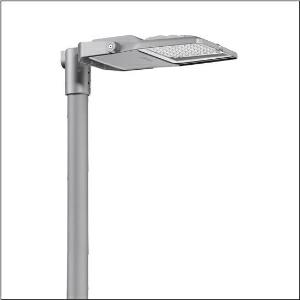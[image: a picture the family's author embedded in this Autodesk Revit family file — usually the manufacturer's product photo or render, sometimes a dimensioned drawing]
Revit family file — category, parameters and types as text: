
# Revit family: floodlight_fl_21_iq_mini___pl64_5xa7771d2e3a_d262
name_source: partatom
category: Lighting Fixtures
units: mm (PartAtom-declared; Revit-internal decimal feet)

## family parameters
Cut with Voids When Loaded = No
Host = Face
Light Source = No
Part Type = Normal
Room Calculation Point = No
Round Connector Dimension = Use Diameter
Shared = No

## types (1)
- --- (1 x LED, 17220 lm, 143 W, 3000K)
    Apparent Load = 143 VA
    CIE Flux Codes = 28 80 98 100 100
    Color Rendering = 70
    Color Temperature = 3000K
    Default Elevation = 1800 mm
    Description = Floodlight FL 21 iQ mini, floodlight, primary light control with lens, of PMMA, primary optical cover: protective disc, of toughened safety glass, transparent, light distribution: PL64, light emission: direct distribution, installation type: surface-mounted, LED, High Power LED, rated luminous flux: 17.220lm, luminous efficacy: 120lm/W, light colour: 730, colour temperature: 3000K, control: Auto-Match, Temp-Guard, Lumen-Switch, Night-Set, Smart-Wire, Light-Fading, Desk-Remote (wireless, voltage-free reading and setting of iQ features in the workshop via application-optimized NFC function/RFID function), optimised constant luminous flux control (CLO 2.0), with terminal, 6-pole, mains connection: 220..240V, AC, 50/60Hz, start of lifetime: 143W, end of service life: 152W, reduction: 61W, luminaire housing, of diecast aluminium, powder-coated, Siteco® metallic grey (DB 702S), corrosivity category C5 mid according to DIN EN ISO 12944, sealing non-destructively replaceable, please order mast flange separately, mast bracket, of steel, galvanised, powder-coated, Siteco® metallic grey (DB 702S), protection rating (complete): IP66, insulation class (complete): insulation class II (safety insulation), certification: CE, ENEC, VDE, protection symbol: D, impact resistance: IK08, permissible operating ambient temperature: -40..+40°C, permissible operating ambient temperature for outdoor applications: -40..+50°C, standard: DIN EN 12944, LABS conformity tested according to VDMA 24364:2018-05, packaging unit: 1 piece

Light Distribution: PL64
    Height = 70 mm
    Lamp = 1 x LED
    Lamp Light Flux = 17220 lm
    Lamp Power = 143 W
    Lamp count = 1
    Length = 485 mm
    Luminous efficacy = 120 lm/W
    Manufacturer = Siteco
    ModVariant = No
    Model = 5XA7771D2E3A
    Number of Poles = 1
    OnlyDefault = Yes
    Power Factor = 1
    Product Name = Floodlight FL 21 iQ mini | PL64
    Product group = floodlight | pylon annexe
    ProductGroupID = 6200
    Protection Class = Protection class II
    Protection Degree = IP 66
    RLX_Detail_Level = 1
    RLX_Emergency_Light_Flux = 0 lm
    RLX_Emergency_Type = 0
    RLX_Emergency_Type_DB = No
    RlxData = <blob elided: 101569 chars, md5=6303d436>
    Socket = socket
    Standby Power = 0 W
    System Light Flux = 17220 lm
    System Power = 143 W
    Type Comments = factory setting: luminous flux: 100 % | dim-lin: 254 | 730 mA
    Type Image = l_1007125.jpg
    URL = http://relux.com
    VarID = @adj_136401
    Voltage = 0 V
    Weight = 0.00 kg
    Width = 337 mm

## geometry (parser evidence)
native form markers: Blend x4, Sweep x12
no freeform markers — native parametric forms only
